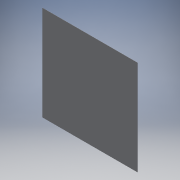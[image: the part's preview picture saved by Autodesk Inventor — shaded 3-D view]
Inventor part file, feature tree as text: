
AUTODESK INVENTOR PART (.ipt)
format: ipt  version: 2018 (Build 220112000, 112)  size: 91,648 bytes
history: native  units: in
note: dims shown in document units (in); Inventor stores cm internally (conversion verified against a paired STEP export)
features: extrude x1, sketch x1
ambient origin geometry x8: Origin, YZ Plane, XZ Plane, XY Plane, X Axis, Y Axis, Z Axis, Center Point
bodies: Solid1 (feature_tree)
feature tree (2):
  extrude  "Carpet"  Depth=168.0in
  sketch  "Sketch1"  dims[d0=168.0in d1=168.0in d2=0.25in d3=0.0in]
